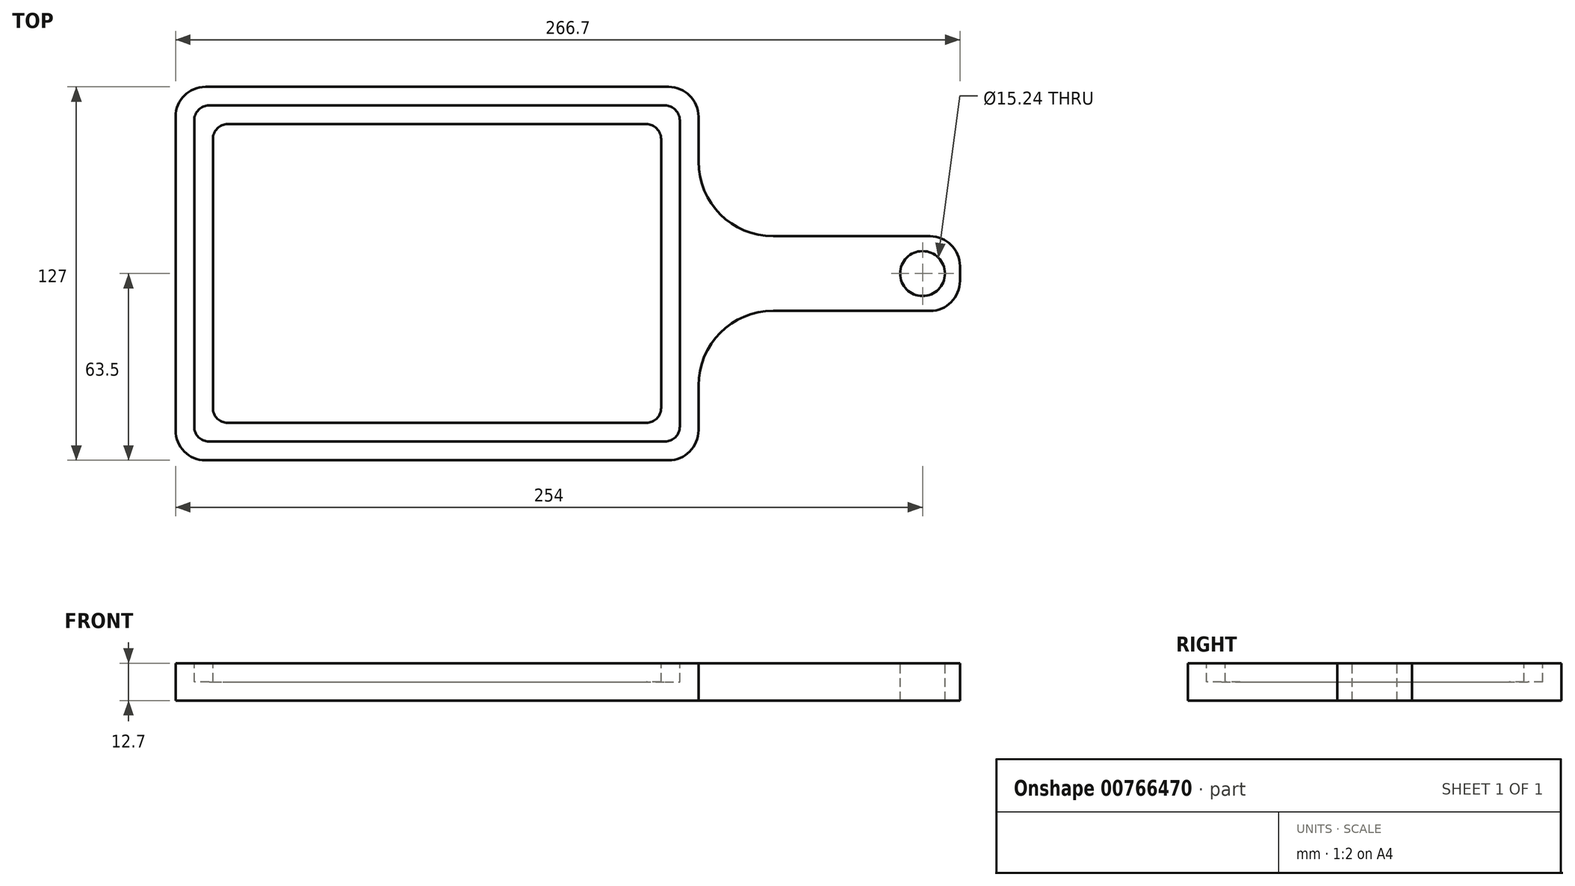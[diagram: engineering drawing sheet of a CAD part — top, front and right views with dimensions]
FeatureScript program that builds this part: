
annotation { "Feature Type Name" : "Feature", "Feature Type Description" : "" }
export const myFeature = defineFeature(function(context is Context, id is Id, definition is map)
    precondition{}
    {
        {
            var Q0;
            Q0=qCreatedBy(makeId("Top.planeOp"),FACE);
            var sketch = newSketch(context, id + "F0", { "sketchPlane" : qUnion([Q0])});
            skLineSegment(sketch, "E0.bottom", {"start": v(0, 0) * mm, "end": v(177.8, 0) * mm});
            skLineSegment(sketch, "E0.top", {"start": v(0, 127) * mm, "end": v(177.8, 127) * mm});
            skLineSegment(sketch, "E0.left", {"start": v(0, 0) * mm, "end": v(0, 127) * mm});
            skLineSegment(sketch, "E0.right", {"start": v(177.8, 0) * mm, "end": v(177.8, 127) * mm});
            skLineSegment(sketch, "E1.bottom", {"start": v(177.8, 76.2) * mm, "end": v(266.7, 76.2) * mm});
            skLineSegment(sketch, "E1.top", {"start": v(177.8, 50.8) * mm, "end": v(266.7, 50.8) * mm});
            skLineSegment(sketch, "E1.left", {"start": v(177.8, 76.2) * mm, "end": v(177.8, 50.8) * mm});
            skLineSegment(sketch, "E1.right", {"start": v(266.7, 76.2) * mm, "end": v(266.7, 50.8) * mm});
            skSolve(sketch);
        }
        {
            var Q0;
            {var subQ1=sQuery(id+"F0.wireOp",EDGE,"E0.bottom");Q0=makeQuery(id+"F0.imprint","IMPRINT",FACE,{"disambiguationData":[TD([[makeQuery(id+"F0.imprint","IMPRINT",EDGE,{"derivedFrom":subQ1}),1.0]])]});}
            var Q1;
            Q1=makeQuery(id+"F0.imprint","IMPRINT",FACE,{"disambiguationData":[TD([[makeQuery(id+"F0.imprint","IMPRINT",EDGE,{"derivedFrom":sQuery(id+"F0.wireOp",EDGE,"E1.bottom")}),-1.0]])]});
            extrude(context, id + "F1", {"entities" : qUnion([Q0, Q1]), "depth" : 12.7 * mm, "offsetDistance" : 25.4 * mm});
        }
        {
            var Q0;
            Q0=makeQuery(id+"F1.opExtrude","CAP_FACE",FACE,{"disambiguationData":[OSD([sQuery(id+"F0.wireOp",EDGE,"E0.bottom"),sQuery(id+"F0.wireOp",EDGE,"E0.top"),sQuery(id+"F0.wireOp",EDGE,"E0.left"),sQuery(id+"F0.wireOp",EDGE,"E0.right"),sQuery(id+"F0.wireOp",EDGE,"E1.bottom"),sQuery(id+"F0.wireOp",EDGE,"E1.top"),sQuery(id+"F0.wireOp",EDGE,"E1.right")])],"isStart":false});
            var sketch = newSketch(context, id + "F2", { "sketchPlane" : qUnion([Q0])});
            skCircle(sketch, "E2", {"center": v(254, 63.5) * mm, "radius": 7.62 * mm});
            skSolve(sketch);
        }
        {
            var Q0;
            Q0 = qSketchRegion(id + "F2", true);
            extrude(context, id + "F3", {"entities" : qUnion([Q0]), "operationType" : NewBodyOperationType.REMOVE, "oppositeDirection" : true, "depth" : 48.26 * mm, "offsetDistance" : 25.4 * mm});
        }
        {
            var Q0;
            Q0=makeQuery(id+"F1.opExtrude","CAP_FACE",FACE,{"disambiguationData":[OSD([sQuery(id+"F0.wireOp",EDGE,"E0.bottom"),sQuery(id+"F0.wireOp",EDGE,"E0.top"),sQuery(id+"F0.wireOp",EDGE,"E0.left"),sQuery(id+"F0.wireOp",EDGE,"E0.right"),sQuery(id+"F0.wireOp",EDGE,"E1.bottom"),sQuery(id+"F0.wireOp",EDGE,"E1.top"),sQuery(id+"F0.wireOp",EDGE,"E1.right")])],"isStart":false});
            var sketch = newSketch(context, id + "F4", { "sketchPlane" : qUnion([Q0])});
            skLineSegment(sketch, "E3.0", {"start": v(6.35, 120.65) * mm, "end": v(171.45, 120.65) * mm});
            skLineSegment(sketch, "E4.0", {"start": v(-6.35, -6.35) * mm, "end": v(184.15, -6.35) * mm});
            skLineSegment(sketch, "E4.1", {"start": v(-6.35, 133.35) * mm, "end": v(-6.35, -6.35) * mm});
            skLineSegment(sketch, "E4.2", {"start": v(184.15, -6.35) * mm, "end": v(184.15, 44.45) * mm});
            skLineSegment(sketch, "E4.3", {"start": v(184.15, 133.35) * mm, "end": v(-6.35, 133.35) * mm});
            skLineSegment(sketch, "E4.4", {"start": v(184.15, 44.45) * mm, "end": v(273.05, 44.45) * mm});
            skLineSegment(sketch, "E4.5", {"start": v(273.05, 44.45) * mm, "end": v(273.05, 82.55) * mm});
            skLineSegment(sketch, "E4.6", {"start": v(273.05, 82.55) * mm, "end": v(184.15, 82.55) * mm});
            skLineSegment(sketch, "E4.7", {"start": v(184.15, 82.55) * mm, "end": v(184.15, 133.35) * mm});
            skLineSegment(sketch, "E5.0", {"start": v(171.45, 76.2) * mm, "end": v(171.45, 120.65) * mm});
            skLineSegment(sketch, "E5.1", {"start": v(171.45, 6.35) * mm, "end": v(171.45, 50.8) * mm});
            skLineSegment(sketch, "E5.2", {"start": v(6.35, 6.35) * mm, "end": v(171.45, 6.35) * mm});
            skLineSegment(sketch, "E5.3", {"start": v(6.35, 6.35) * mm, "end": v(6.35, 120.65) * mm});
            skLineSegment(sketch, "E6", {"start": v(171.45, 76.2) * mm, "end": v(171.45, 50.8) * mm});
            skLineSegment(sketch, "E7.0", {"start": v(12.7, 12.7) * mm, "end": v(12.7, 114.3) * mm});
            skLineSegment(sketch, "E7.1", {"start": v(165.1, 76.2) * mm, "end": v(165.1, 114.3) * mm});
            skLineSegment(sketch, "E7.2", {"start": v(165.1, 76.2) * mm, "end": v(165.1, 50.8) * mm});
            skLineSegment(sketch, "E7.3", {"start": v(12.7, 114.3) * mm, "end": v(165.1, 114.3) * mm});
            skLineSegment(sketch, "E7.4", {"start": v(165.1, 12.7) * mm, "end": v(165.1, 50.8) * mm});
            skLineSegment(sketch, "E7.5", {"start": v(12.7, 12.7) * mm, "end": v(165.1, 12.7) * mm});
            skSolve(sketch);
        }
        {
            var Q0;
            Q0=makeQuery(id+"F4.imprint","IMPRINT",FACE,{"disambiguationData":[TD([[makeQuery(id+"F4.imprint","IMPRINT",EDGE,{"derivedFrom":sQuery(id+"F4.wireOp",EDGE,"E5.0")}),1.0]])]});
            extrude(context, id + "F5", {"entities" : qUnion([Q0]), "operationType" : NewBodyOperationType.REMOVE, "oppositeDirection" : true, "depth" : 6.35 * mm, "offsetDistance" : 25.4 * mm});
        }
        {
            var Q0;
            Q0=makeQuery(id+"F5.boolean.opBoolean","COPY",EDGE,{"derivedFrom":makeQuery(id+"F5.opExtrude","SWEPT_EDGE",EDGE,{"disambiguationData":[OSD([sQuery(id+"F4.wireOp",EDGE,"E5.2"),sQuery(id+"F4.wireOp",EDGE,"E5.3")])]})});
            var Q1;
            Q1=makeQuery(id+"F5.boolean.opBoolean","COPY",EDGE,{"derivedFrom":makeQuery(id+"F5.opExtrude","SWEPT_EDGE",EDGE,{"disambiguationData":[OSD([sQuery(id+"F4.wireOp",EDGE,"E5.1"),sQuery(id+"F4.wireOp",EDGE,"E5.2")])]})});
            var Q2;
            Q2=makeQuery(id+"F5.boolean.opBoolean","COPY",EDGE,{"derivedFrom":makeQuery(id+"F5.opExtrude","SWEPT_EDGE",EDGE,{"disambiguationData":[OSD([sQuery(id+"F4.wireOp",EDGE,"E5.0"),sQuery(id+"F4.wireOp",EDGE,"E3.0")])]})});
            var Q3;
            Q3=makeQuery(id+"F5.boolean.opBoolean","COPY",EDGE,{"derivedFrom":makeQuery(id+"F5.opExtrude","SWEPT_EDGE",EDGE,{"disambiguationData":[OSD([sQuery(id+"F4.wireOp",EDGE,"E5.3"),sQuery(id+"F4.wireOp",EDGE,"E3.0")])]})});
            var Q4;
            Q4=makeQuery(id+"F5.boolean.opBoolean","COPY",EDGE,{"derivedFrom":makeQuery(id+"F5.opExtrude","SWEPT_EDGE",EDGE,{"disambiguationData":[OSD([sQuery(id+"F4.wireOp",EDGE,"E7.4"),sQuery(id+"F4.wireOp",EDGE,"E7.5")])]})});
            var Q5;
            Q5=makeQuery(id+"F5.boolean.opBoolean","COPY",EDGE,{"derivedFrom":makeQuery(id+"F5.opExtrude","SWEPT_EDGE",EDGE,{"disambiguationData":[OSD([sQuery(id+"F4.wireOp",EDGE,"E7.1"),sQuery(id+"F4.wireOp",EDGE,"E7.3")])]})});
            var Q6;
            Q6=makeQuery(id+"F5.boolean.opBoolean","COPY",EDGE,{"derivedFrom":makeQuery(id+"F5.opExtrude","SWEPT_EDGE",EDGE,{"disambiguationData":[OSD([sQuery(id+"F4.wireOp",EDGE,"E7.0"),sQuery(id+"F4.wireOp",EDGE,"E7.3")])]})});
            var Q7;
            Q7=makeQuery(id+"F5.boolean.opBoolean","COPY",EDGE,{"derivedFrom":makeQuery(id+"F5.opExtrude","SWEPT_EDGE",EDGE,{"disambiguationData":[OSD([sQuery(id+"F4.wireOp",EDGE,"E7.0"),sQuery(id+"F4.wireOp",EDGE,"E7.5")])]})});
            fillet(context, id + "F6", {"entities" : qUnion([Q0, Q1, Q2, Q3, Q4, Q5, Q6, Q7]), "radius" : 5.08 * mm, "tangentPropagation" : true, "allowEdgeOverflow" : false});
        }
        {
            var Q0;
            Q0=makeQuery(id+"F1.opExtrude","SWEPT_EDGE",EDGE,{"disambiguationData":[OSD([sQuery(id+"F0.wireOp",EDGE,"E0.right"),sQuery(id+"F0.wireOp",EDGE,"E1.top"),sQuery(id+"F0.wireOp",EDGE,"E1.left")])]});
            var Q1;
            Q1=makeQuery(id+"F1.opExtrude","SWEPT_EDGE",EDGE,{"disambiguationData":[OSD([sQuery(id+"F0.wireOp",EDGE,"E0.right"),sQuery(id+"F0.wireOp",EDGE,"E1.bottom"),sQuery(id+"F0.wireOp",EDGE,"E1.left")])]});
            fillet(context, id + "F7", {"entities" : qUnion([Q0, Q1]), "radius" : 25.4 * mm, "tangentPropagation" : true, "allowEdgeOverflow" : false});
        }
        {
            var Q0;
            Q0=makeQuery(id+"F1.opExtrude","SWEPT_EDGE",EDGE,{"disambiguationData":[OSD([sQuery(id+"F0.wireOp",EDGE,"E1.top"),sQuery(id+"F0.wireOp",EDGE,"E1.right")])]});
            var Q1;
            Q1=makeQuery(id+"F1.opExtrude","SWEPT_EDGE",EDGE,{"disambiguationData":[OSD([sQuery(id+"F0.wireOp",EDGE,"E1.bottom"),sQuery(id+"F0.wireOp",EDGE,"E1.right")])]});
            var Q2;
            Q2=makeQuery(id+"F1.opExtrude","SWEPT_EDGE",EDGE,{"disambiguationData":[OSD([sQuery(id+"F0.wireOp",EDGE,"E0.bottom"),sQuery(id+"F0.wireOp",EDGE,"E0.right")])]});
            var Q3;
            Q3=makeQuery(id+"F1.opExtrude","SWEPT_EDGE",EDGE,{"disambiguationData":[OSD([sQuery(id+"F0.wireOp",EDGE,"E0.top"),sQuery(id+"F0.wireOp",EDGE,"E0.right")])]});
            var Q4;
            Q4=makeQuery(id+"F1.opExtrude","SWEPT_EDGE",EDGE,{"disambiguationData":[OSD([sQuery(id+"F0.wireOp",EDGE,"E0.top"),sQuery(id+"F0.wireOp",EDGE,"E0.left")])]});
            var Q5;
            Q5=makeQuery(id+"F1.opExtrude","SWEPT_EDGE",EDGE,{"disambiguationData":[OSD([sQuery(id+"F0.wireOp",EDGE,"E0.bottom"),sQuery(id+"F0.wireOp",EDGE,"E0.left")])]});
            fillet(context, id + "F8", {"entities" : qUnion([Q0, Q1, Q2, Q3, Q4, Q5]), "radius" : 10.16 * mm, "tangentPropagation" : true, "allowEdgeOverflow" : false});
        }
    });
